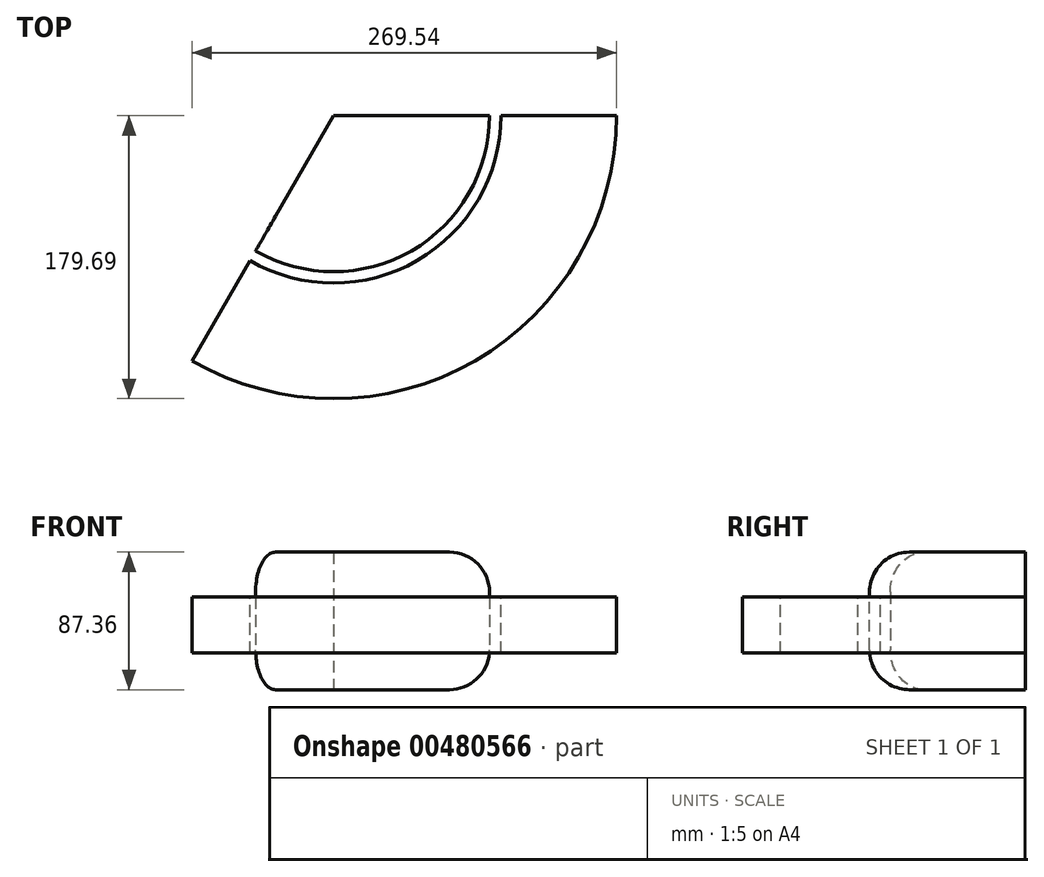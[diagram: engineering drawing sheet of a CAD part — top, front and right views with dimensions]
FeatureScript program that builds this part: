
annotation { "Feature Type Name" : "Feature", "Feature Type Description" : "" }
export const myFeature = defineFeature(function(context is Context, id is Id, definition is map)
    precondition{}
    {
        {
            var Q0;
            Q0=qCreatedBy(makeId("Front.planeOp"),FACE);
            var sketch = newSketch(context, id + "F0", { "sketchPlane" : qUnion([Q0])});
            skLineSegment(sketch, "E0.bottom", {"start": v(-31.74, 48.2) * mm, "end": v(41.9, 48.2) * mm});
            skLineSegment(sketch, "E0.top", {"start": v(-31.74, -39.17) * mm, "end": v(41.9, -39.17) * mm});
            skLineSegment(sketch, "E0.left", {"start": v(-31.74, 48.2) * mm, "end": v(-31.74, -39.17) * mm});
            skLineSegment(sketch, "E0.right", {"start": v(67.3, 22.8) * mm, "end": v(67.3, -13.77) * mm});
            skLineSegment(sketch, "E1.bottom", {"start": v(74.49, -15.9) * mm, "end": v(147.96, -15.9) * mm});
            skLineSegment(sketch, "E1.top", {"start": v(74.49, 19.71) * mm, "end": v(147.96, 19.71) * mm});
            skLineSegment(sketch, "E1.left", {"start": v(74.49, -15.9) * mm, "end": v(74.49, 19.71) * mm});
            skLineSegment(sketch, "E1.right", {"start": v(147.96, -15.9) * mm, "end": v(147.96, 19.71) * mm});
            skLineSegment(sketch, "E2.bottom", {"start": v(128.36, 83.7) * mm, "end": v(53.74, 83.7) * mm});
            skLineSegment(sketch, "E2.top", {"start": v(128.36, 108.85) * mm, "end": v(53.74, 108.85) * mm});
            skLineSegment(sketch, "E2.left", {"start": v(128.36, 83.7) * mm, "end": v(128.36, 108.85) * mm});
            skLineSegment(sketch, "E2.right", {"start": v(53.74, 83.7) * mm, "end": v(53.74, 108.85) * mm});
            skPoint(sketch, "E3.visualSharp", {"position": v(67.3, 48.2) * mm});
            skArc(sketch, "E3.filletArc", {"start": v(67.3, 22.8) * mm, "mid": v(59.86, 40.75) * mm, "end": v(41.9, 48.2) * mm});
            skPoint(sketch, "E4.visualSharp", {"position": v(67.3, -39.17) * mm});
            skArc(sketch, "E4.filletArc", {"start": v(41.9, -39.17) * mm, "mid": v(59.86, -31.73) * mm, "end": v(67.3, -13.77) * mm});
            skSolve(sketch);
        }
        {
            var Q0;
            Q0=makeQuery(id+"F0.imprint","IMPRINT",FACE,{"disambiguationData":[TD([[makeQuery(id+"F0.imprint","IMPRINT",EDGE,{"derivedFrom":sQuery(id+"F0.wireOp",EDGE,"E0.bottom")}),-1.0]])]});
            var Q1;
            Q1=makeQuery(id+"F0.imprint","IMPRINT",FACE,{"disambiguationData":[TD([[makeQuery(id+"F0.imprint","IMPRINT",EDGE,{"derivedFrom":sQuery(id+"F0.wireOp",EDGE,"E1.bottom")}),1.0]])]});
            var Q2;
            Q2=sQuery(id+"F0.wireOp",EDGE,"E0.left");
            revolve(context, id + "F1", {"entities" : qUnion([Q0, Q1]), "axis" : qUnion([Q2]), "revolveType" : RevolveType.TWO_DIRECTIONS, "angle" : 120 * degree, "angleBack" : 0 * degree});
        }
    });
